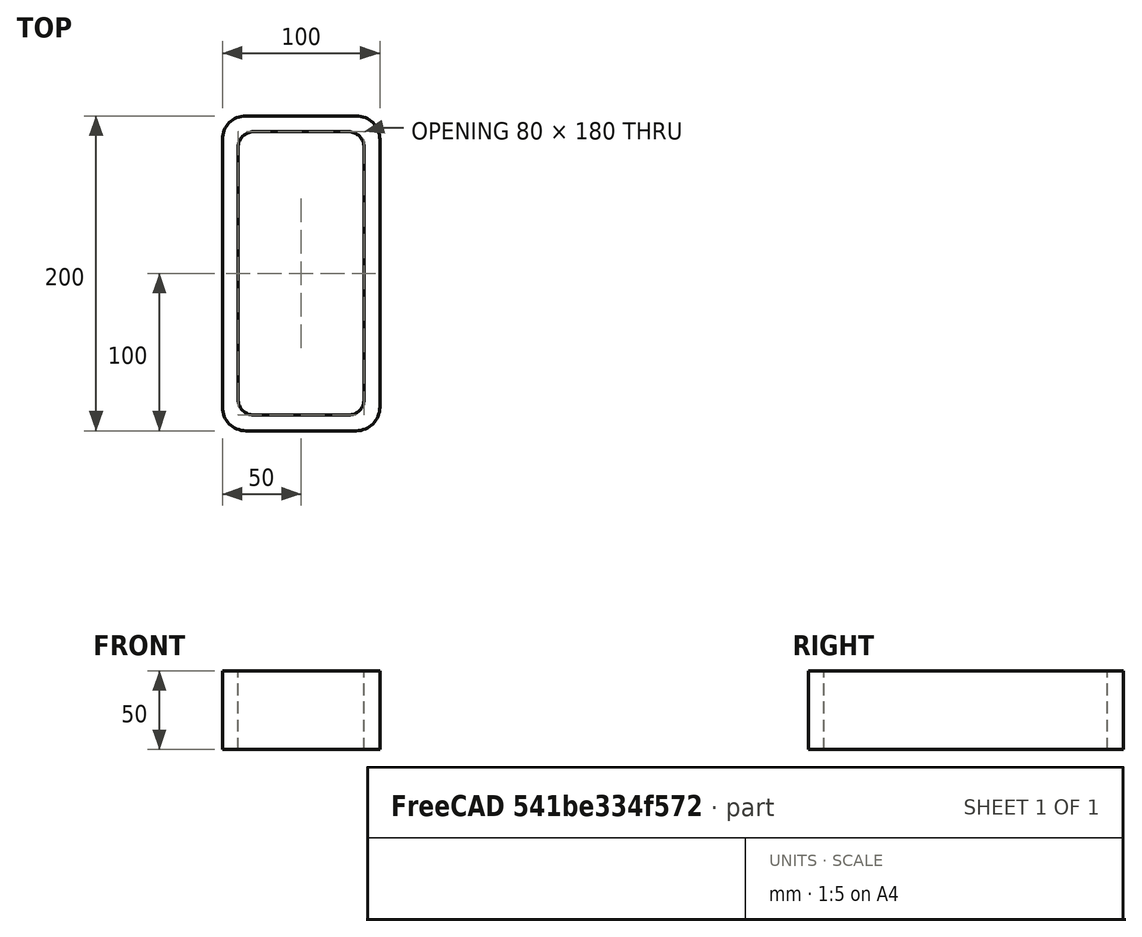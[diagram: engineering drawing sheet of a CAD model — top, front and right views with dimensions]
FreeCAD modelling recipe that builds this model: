
FCSTD DOCUMENT  (FreeCAD 0.15R4671 (Git))
Label: Rectangular hollow section 200x100x10 EN10219 S235JRH
License: All rights reserved
LicenseURL: http://en.wikipedia.org/wiki/All_rights_reserved
objects: Sketcher::SketchObject×1, Part::Extrusion×1
note: 2 computed .brp shape members not serialized (recipe doc carries the construction recipe); baked Part::Feature solids carry a one-line shape summary decoded from their .brp

FEATURE [Sketcher::SketchObject] Sketch
  sketch-geometry (16):
    g0: LineSegment StartX=-30 StartY=90 StartZ=0 EndX=30 EndY=90 EndZ=0
    g1: LineSegment StartX=40 StartY=80 StartZ=0 EndX=40 EndY=-80 EndZ=0
    g2: LineSegment StartX=30 StartY=-90 StartZ=0 EndX=-30 EndY=-90 EndZ=0
    g3: LineSegment StartX=-40 StartY=-80 StartZ=0 EndX=-40 EndY=80 EndZ=0
    g4: LineSegment StartX=-35 StartY=100 StartZ=0 EndX=35 EndY=100 EndZ=0
    g5: LineSegment StartX=50 StartY=85 StartZ=0 EndX=50 EndY=-85 EndZ=0
    g6: LineSegment StartX=35 StartY=-100 StartZ=0 EndX=-35 EndY=-100 EndZ=0
    g7: LineSegment StartX=-50 StartY=-85 StartZ=0 EndX=-50 EndY=85 EndZ=0
    g8: ArcOfCircle CenterX=-30 CenterY=80 CenterZ=0 NormalX=0 NormalY=0 NormalZ=1 Radius=10 StartAngle=1.5708 EndAngle=3.14159
    g9: ArcOfCircle CenterX=30 CenterY=80 CenterZ=0 NormalX=0 NormalY=0 NormalZ=1 Radius=10 StartAngle=0 EndAngle=1.5708
    g10: ArcOfCircle CenterX=30 CenterY=-80 CenterZ=0 NormalX=0 NormalY=0 NormalZ=1 Radius=10 StartAngle=4.71239 EndAngle=6.28319
    g11: ArcOfCircle CenterX=-30 CenterY=-80 CenterZ=0 NormalX=0 NormalY=0 NormalZ=1 Radius=10 StartAngle=3.14159 EndAngle=4.71239
    g12: ArcOfCircle CenterX=35 CenterY=85 CenterZ=0 NormalX=0 NormalY=0 NormalZ=1 Radius=15 StartAngle=0 EndAngle=1.5708
    g13: ArcOfCircle CenterX=35 CenterY=-85 CenterZ=0 NormalX=0 NormalY=0 NormalZ=1 Radius=15 StartAngle=4.71239 EndAngle=6.28319
    g14: ArcOfCircle CenterX=-35 CenterY=-85 CenterZ=0 NormalX=0 NormalY=0 NormalZ=1 Radius=15 StartAngle=3.14159 EndAngle=4.71239
    g15: ArcOfCircle CenterX=-35 CenterY=85 CenterZ=0 NormalX=0 NormalY=0 NormalZ=1 Radius=15 StartAngle=1.5708 EndAngle=3.14159
  constraints (36):
    c: Horizontal(g2)
    c: Vertical(g3)
    c: Horizontal(g6)
    c: Vertical(g7)
    c: Tangent(g3,g8) = 1.5708
    c: Tangent(g0,g8) = 1.5708
    c: Tangent(g0,g9) = 1.5708
    c: Tangent(g1,g9) = 1.5708
    c: Tangent(g1,g10) = 1.5708
    c: Tangent(g2,g10) = 1.5708
    c: Tangent(g2,g11) = 1.5708
    c: Tangent(g3,g11) = 1.5708
    c: Tangent(g4,g12) = 1.5708
    c: Tangent(g5,g12) = 1.5708
    c: Tangent(g5,g13) = 1.5708
    c: Tangent(g6,g13) = 1.5708
    c: Tangent(g6,g14) = 1.5708
    c: Tangent(g7,g14) = 1.5708
    c: Tangent(g7,g15) = 1.5708
    c: Tangent(g4,g15) = 1.5708
    c: Equal(g9,g8)
    c: Equal(g9,g11)
    c: Equal(g9,g10)
    c: Equal(g12,g15)
    c: Equal(g12,g14)
    c: Equal(g12,g13)
    c: Symmetric(g4,g6,g-1)
    c: Symmetric(g7,g5,g-2)
    c: DistanceY(g4,g6) = -200
    c: DistanceX(g7,g5) = 100
    c: Symmetric(g3,g1,g-2)
    c: Symmetric(g0,g2,g-1)
    c: DistanceY(g0,g4) = 10
    c: DistanceX(g5,g1) = -10
    c: Radius(g9) = 10
    c: Radius(g12) = 15
FEATURE [Part::Extrusion] Extrude  label="Rectangular hollow section 200x100x10 EN10219 S235JRH"
  Base = -> Sketch
  Dir = (0,0,50)
  Solid = true
